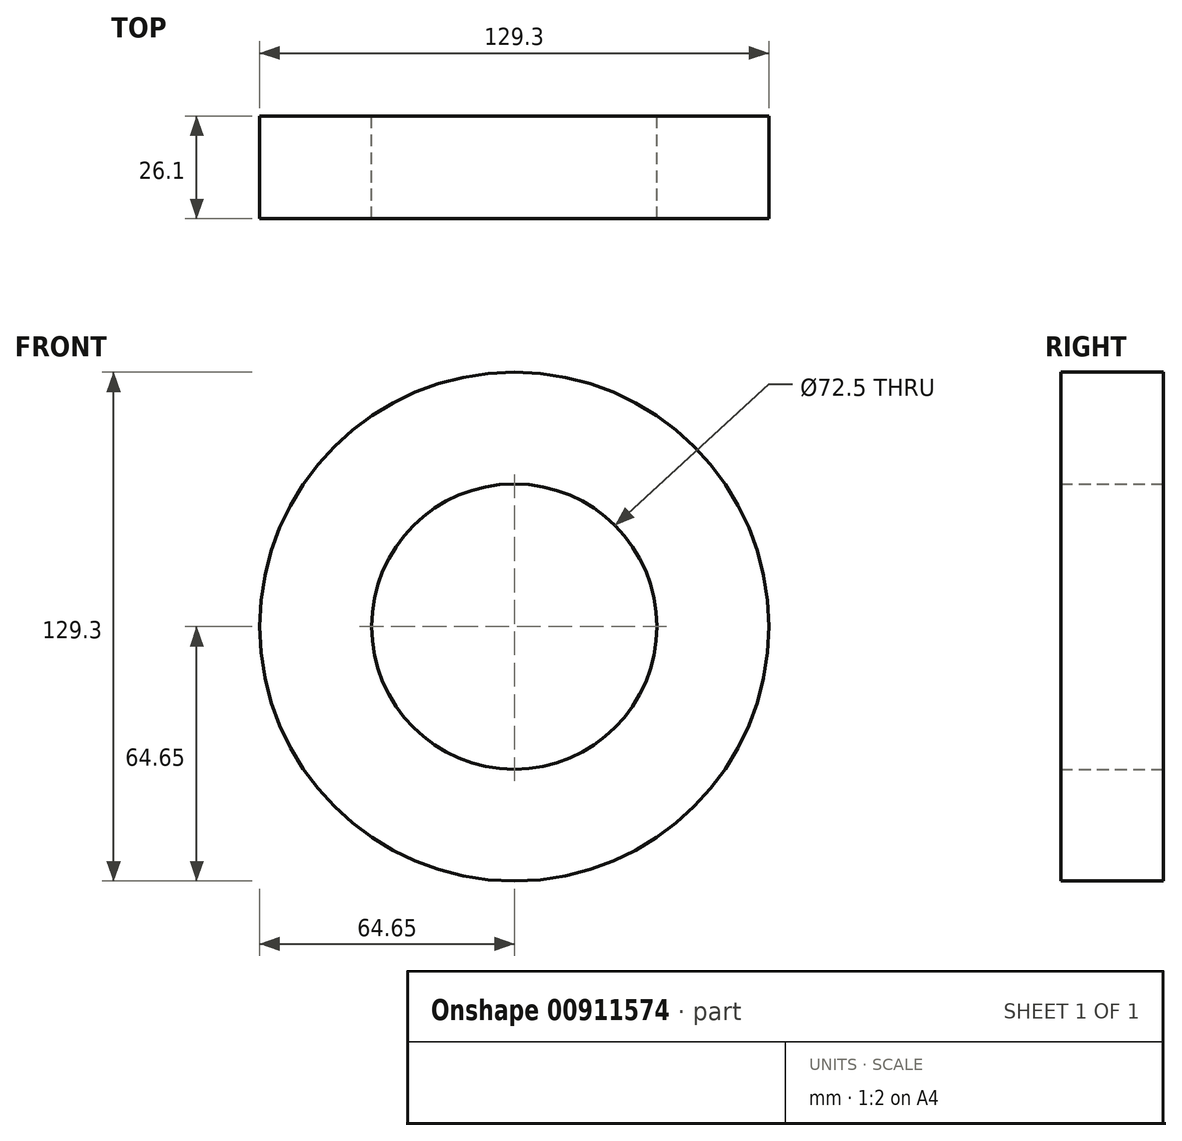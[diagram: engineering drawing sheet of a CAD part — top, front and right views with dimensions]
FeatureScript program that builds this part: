
annotation { "Feature Type Name" : "Feature", "Feature Type Description" : "" }
export const myFeature = defineFeature(function(context is Context, id is Id, definition is map)
    precondition{}
    {
        {
            var Q0;
            Q0=qCreatedBy(makeId("Front.planeOp"),FACE);
            var sketch = newSketch(context, id + "F0", { "sketchPlane" : qUnion([Q0])});
            skCircle(sketch, "E0", {"center": v(0, 0) * mm, "radius": 64.65 * mm});
            skCircle(sketch, "E1", {"center": v(0, 0) * mm, "radius": 36.25 * mm});
            skSolve(sketch);
        }
        {
            var Q0;
            Q0=makeQuery(id+"F0.imprint","IMPRINT",FACE,{"disambiguationData":[TD([[makeQuery(id+"F0.imprint","IMPRINT",EDGE,{"derivedFrom":sQuery(id+"F0.wireOp",EDGE,"E0")}),1.0]])]});
            extrude(context, id + "F1", {"entities" : qUnion([Q0]), "depth" : 26.1 * mm, "offsetDistance" : 25 * mm});
        }
    });
